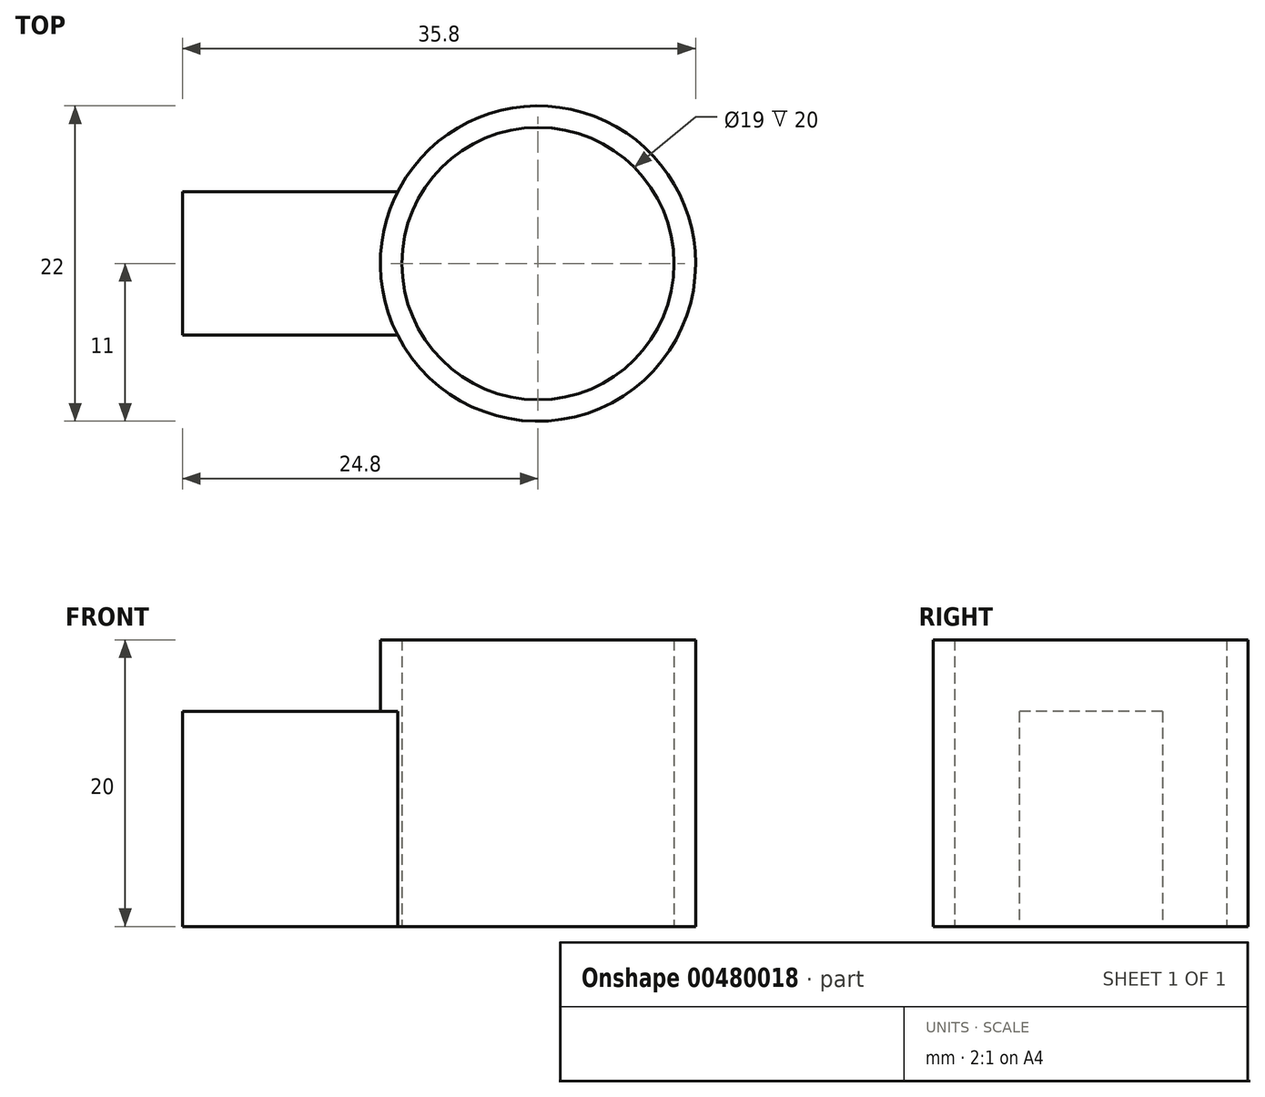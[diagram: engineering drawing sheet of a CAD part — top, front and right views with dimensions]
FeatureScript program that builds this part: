
annotation { "Feature Type Name" : "Feature", "Feature Type Description" : "" }
export const myFeature = defineFeature(function(context is Context, id is Id, definition is map)
    precondition{}
    {
        {
            var Q0;
            Q0=qCreatedBy(makeId("Top.planeOp"),FACE);
            var sketch = newSketch(context, id + "F0", { "sketchPlane" : qUnion([Q0])});
            skLineSegment(sketch, "E0.bottom", {"start": v(-24.8, 5) * mm, "end": v(-9.8, 5) * mm});
            skLineSegment(sketch, "E0.top", {"start": v(-24.8, -5) * mm, "end": v(-9.8, -5) * mm});
            skLineSegment(sketch, "E0.left", {"start": v(-24.8, 5) * mm, "end": v(-24.8, -5) * mm});
            skCircle(sketch, "E1", {"center": v(0, 0) * mm, "radius": 11 * mm});
            skCircle(sketch, "E2", {"center": v(0, 0) * mm, "radius": 9.5 * mm});
            skLineSegment(sketch, "E3.bottom", {"start": v(-142.59, 34.43) * mm, "end": v(-123.94, 34.43) * mm});
            skLineSegment(sketch, "E3.top", {"start": v(-142.59, 34.11) * mm, "end": v(-123.94, 34.11) * mm});
            skLineSegment(sketch, "E3.left", {"start": v(-142.59, 34.43) * mm, "end": v(-142.59, 34.11) * mm});
            skLineSegment(sketch, "E3.right", {"start": v(-123.94, 34.43) * mm, "end": v(-123.94, 34.11) * mm});
            skSolve(sketch);
        }
        {
            var Q0;
            Q0=makeQuery(id+"F0.imprint","IMPRINT",FACE,{"disambiguationData":[TD([[makeQuery(id+"F0.imprint","IMPRINT",EDGE,{"derivedFrom":sQuery(id+"F0.wireOp",EDGE,"E2")}),-1.0]])]});
            extrude(context, id + "F1", {"entities" : qUnion([Q0]), "depth" : 20 * mm});
        }
        {
            var Q0;
            {var subQ0=sQuery(id+"F0.wireOp",EDGE,"E0.bottom");Q0=makeQuery(id+"F0.imprint","IMPRINT",FACE,{"disambiguationData":[TD([[makeQuery(id+"F0.imprint","IMPRINT",EDGE,{"derivedFrom":subQ0}),-1.0]])]});}
            extrude(context, id + "F2", {"entities" : qUnion([Q0]), "operationType" : NewBodyOperationType.ADD, "depth" : 15 * mm});
        }
    });
